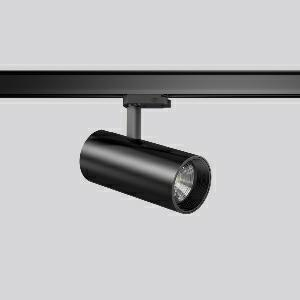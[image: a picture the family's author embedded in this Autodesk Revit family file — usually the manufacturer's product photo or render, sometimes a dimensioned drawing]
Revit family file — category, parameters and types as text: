
# Revit family: deecos_s_mini_742200_003_3_76_c2b4
name_source: partatom
category: Lighting Fixtures
units: mm (PartAtom-declared; Revit-internal decimal feet)

## family parameters
Cut with Voids When Loaded = No
Host = Face
Light Source = No
Part Type = Normal
Room Calculation Point = No
Round Connector Dimension = Use Diameter
Shared = No

## types (1)
- DEECOS S mini (1 x LED Modul 935, 2000 lm, 3500)
    Apparent Load = 20 VA
    Approval mark = CE
    CIE Flux Codes = 98 100 100 100 100
    Color Rendering = 92
    Color Temperature = 3500
    Default Elevation = 1800 mm
    Description = Series: DEECOS S mini
LED surface-mounted projector in modern design with no visible cooling ribs. Housing: die-cast aluminium, powder-coated. Rotation range: 356°. Swivel range: 90°. Black plastic ring and recessed LED to prevent glare from the side. Optical assembly with lens made of plastic (polycarbonate) for the best homogeneous light distribution - can be changed without tools. Best colour rendering index Ra>90. With adapter for RZB 3-circuit DALI tracks. Suitable for Track on ceiling, Wall track. High quality converter without flickering and stroboscopic effect. The following accessories can be mounted without use of tools: interchangeable lenses, decorative glasses, honeycomb louvre, clear and frosted diffusers, white interchangeable plastic ring. 
Colour: deep black, matt (RAL 9005)
Diameter: 87 mm
Height: 214 mm
Lamp: LED
Socket: without socket
Colour temperature: 3500K
Colour rendering index (CRI): 92
System power: 20 W
Rated luminous flux: 2000 lm
Luminous efficiency: 100 lm/W
Control gear: Converter, dimmable, DALI
Protection class: I
Type of protection: IP 20
    Height = 214 mm
    Lamp = 1 x LED Modul 935
    Lamp Light Flux = 2000 lm
    Lamp count = 1
    Length = 87 mm
    Lifetime = 50000 h
    Luminous efficacy = 100 lm/W
    Manufacturer = RZB
    ModVariant = No
    Model = 742200.003.3.76
    Mounting Place = Ceiling
    Mounting Type = Rail mounted
    Number of Poles = 1
    OnlyDefault = Yes
    Power Factor = 1
    Product Name = DEECOS S mini
    Product group = Track mounted projectors
    ProductGroupID = 301
    Protection Class = Protection class I
    Protection Degree = IP 20
    RLX_Detail_Level = 1
    RLX_Emergency_Light_Flux = 0 lm
    RLX_Emergency_Type = 0
    RLX_Emergency_Type_DB = No
    RlxData = <blob elided: 38825 chars, md5=b0b3e5c0>
    Socket = socket
    Standby Power = 0 W
    System Light Flux = 2000 lm
    System Power = 20 W
    Type Comments = Product without accessories
    Type Image = 741930.003.jpg
    URL = http://relux.com
    VarID = ---
    Voltage = 230 V
    Voltage Range = 220-240 V
    Weight = 0.00 kg
    Width = 0 mm  [stored 0 ft]

note: [stored X ft] marks values corroborated as IEEE doubles in the binary element streams (Revit-internal decimal feet)

## geometry (parser evidence)
native form markers: Blend x4, Sweep x10
no freeform markers — native parametric forms only
